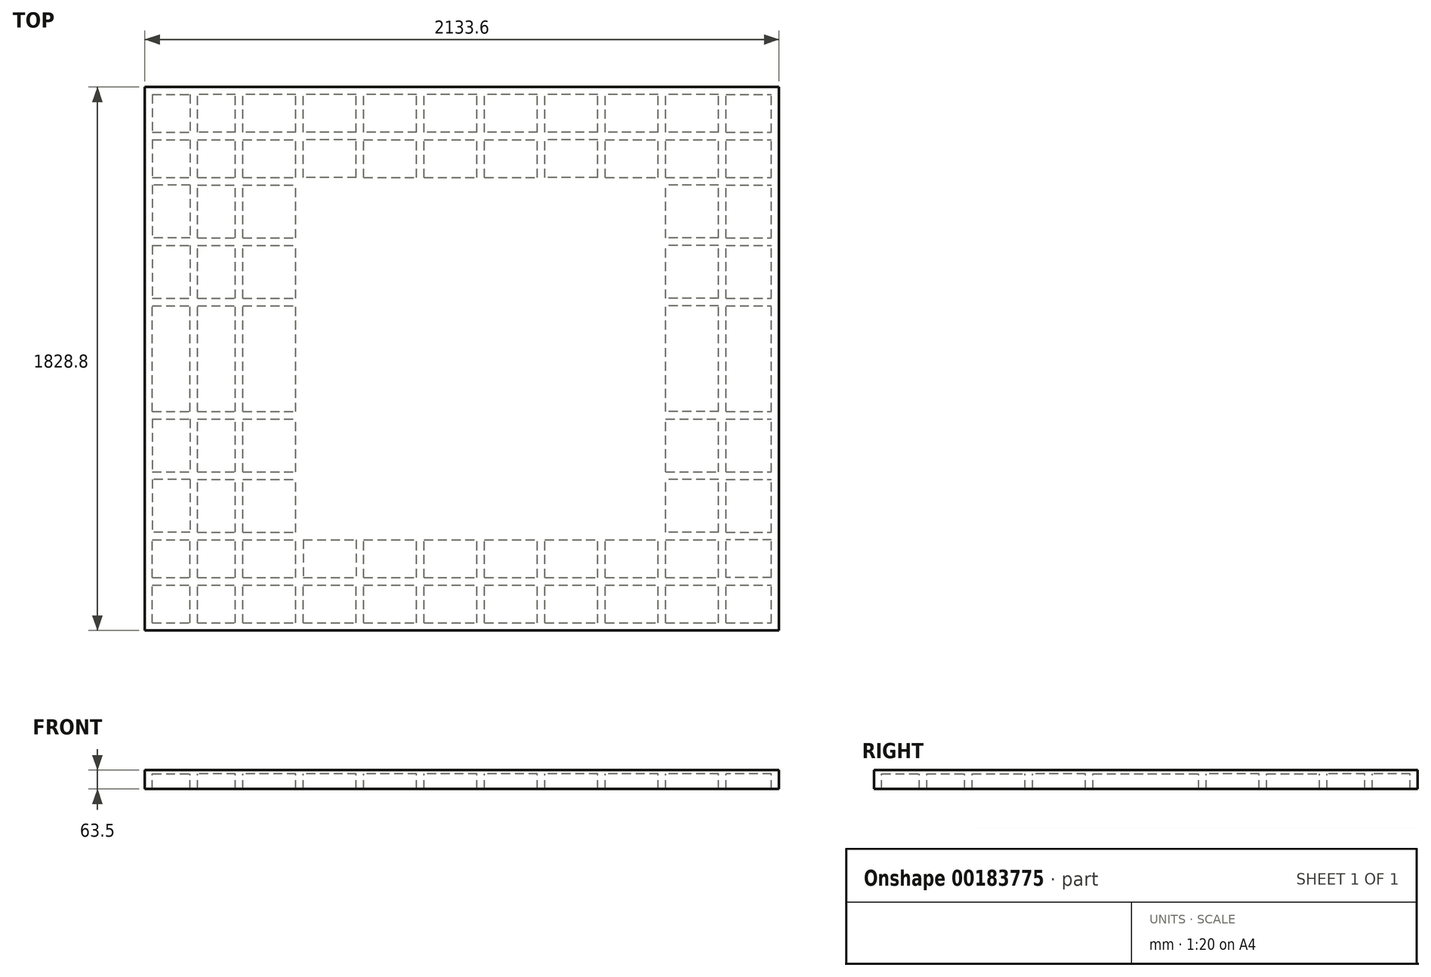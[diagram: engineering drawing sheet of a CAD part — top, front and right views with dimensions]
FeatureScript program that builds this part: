
annotation { "Feature Type Name" : "Feature", "Feature Type Description" : "" }
export const myFeature = defineFeature(function(context is Context, id is Id, definition is map)
    precondition{}
    {
        {
            var Q0;
            Q0=qCreatedBy(makeId("Top.planeOp"),FACE);
            var sketch = newSketch(context, id + "F0", { "sketchPlane" : qUnion([Q0])});
            skLineSegment(sketch, "E0.bottom", {"start": v(0, 0) * mm, "end": v(-2133.6, 0) * mm});
            skLineSegment(sketch, "E0.top", {"start": v(0, 1828.8) * mm, "end": v(-2133.6, 1828.8) * mm});
            skLineSegment(sketch, "E0.left", {"start": v(0, 0) * mm, "end": v(0, 1828.8) * mm});
            skLineSegment(sketch, "E0.right", {"start": v(-2133.6, 0) * mm, "end": v(-2133.6, 1828.8) * mm});
            skSolve(sketch);
        }
        {
            var Q0;
            Q0 = qSketchRegion(id + "F0", true);
            extrude(context, id + "F1", {"entities" : qUnion([Q0]), "oppositeDirection" : true, "depth" : 12.7 * mm});
        }
        {
            var Q0;
            Q0=makeQuery(id+"F1.opExtrude","CAP_FACE",FACE,{"disambiguationData":[OSD([sQuery(id+"F0.wireOp",EDGE,"E0.bottom"),sQuery(id+"F0.wireOp",EDGE,"E0.top"),sQuery(id+"F0.wireOp",EDGE,"E0.left"),sQuery(id+"F0.wireOp",EDGE,"E0.right")])],"isStart":false});
            var sketch = newSketch(context, id + "F2", { "sketchPlane" : qUnion([Q0])});
            skLineSegment(sketch, "E1", {"start": v(-2133.6, 0) * mm, "end": v(-2133.6, -1828.8) * mm});
            skLineSegment(sketch, "E2", {"start": v(-2133.6, -1828.8) * mm, "end": v(0, -1828.8) * mm});
            skLineSegment(sketch, "E3", {"start": v(0, -1828.8) * mm, "end": v(0, 0) * mm});
            skLineSegment(sketch, "E4", {"start": v(0, 0) * mm, "end": v(-2133.6, 0) * mm});
            skLineSegment(sketch, "E5", {"start": v(-2133.6, -25.4) * mm, "end": v(0, -25.4) * mm, "construction": true});
            skLineSegment(sketch, "E6", {"start": v(-2133.6, -1803.4) * mm, "end": v(0, -1803.4) * mm, "construction": true});
            skLineSegment(sketch, "E7", {"start": v(-25.4, 0) * mm, "end": v(-25.4, -1828.8) * mm, "construction": true});
            skLineSegment(sketch, "E8", {"start": v(-2108.2, 0) * mm, "end": v(-2108.2, -1828.8) * mm, "construction": true});
            skLineSegment(sketch, "E9", {"start": v(-2133.6, -152.4) * mm, "end": v(0, -152.4) * mm, "construction": true});
            skLineSegment(sketch, "E10", {"start": v(-2133.6, -304.8) * mm, "end": v(0, -304.8) * mm, "construction": true});
            skLineSegment(sketch, "E11", {"start": v(-2133.6, -508) * mm, "end": v(0, -508) * mm, "construction": true});
            skLineSegment(sketch, "E12", {"start": v(-609.6, 0) * mm, "end": v(-609.6, -1828.8) * mm, "construction": true});
            skLineSegment(sketch, "E13", {"start": v(-812.8, 0) * mm, "end": v(-812.8, -1828.8) * mm, "construction": true});
            skLineSegment(sketch, "E14", {"start": v(-1981.2, 0) * mm, "end": v(-1981.2, -1828.8) * mm, "construction": true});
            skLineSegment(sketch, "E15", {"start": v(-1828.8, 0) * mm, "end": v(-1828.8, -1828.8) * mm, "construction": true});
            skLineSegment(sketch, "E16", {"start": v(-1625.6, 0) * mm, "end": v(-1625.6, -1828.8) * mm, "construction": true});
            skLineSegment(sketch, "E17", {"start": v(-1422.4, 0) * mm, "end": v(-1422.4, -1828.8) * mm, "construction": true});
            skLineSegment(sketch, "E18", {"start": v(-1219.2, 0) * mm, "end": v(-1219.2, -1828.8) * mm, "construction": true});
            skLineSegment(sketch, "E19", {"start": v(-1016, 0) * mm, "end": v(-1016, -1828.8) * mm, "construction": true});
            skLineSegment(sketch, "E20", {"start": v(-406.4, 0) * mm, "end": v(-406.4, -1828.8) * mm, "construction": true});
            skLineSegment(sketch, "E21", {"start": v(-203.2, 0) * mm, "end": v(-203.2, -1828.8) * mm, "construction": true});
            skLineSegment(sketch, "E22", {"start": v(0, -1676.4) * mm, "end": v(-2133.6, -1676.4) * mm, "construction": true});
            skLineSegment(sketch, "E23", {"start": v(-2133.6, -1524) * mm, "end": v(0, -1524) * mm, "construction": true});
            skLineSegment(sketch, "E24", {"start": v(-2133.6, -1320.8) * mm, "end": v(0, -1320.8) * mm, "construction": true});
            skLineSegment(sketch, "E25", {"start": v(0, -711.2) * mm, "end": v(-2133.6, -711.2) * mm, "construction": true});
            skLineSegment(sketch, "E26", {"start": v(0, -1117.6) * mm, "end": v(-2133.6, -1117.6) * mm, "construction": true});
            skLineSegment(sketch, "E27.bottom", {"start": v(-2108.2, -25.4) * mm, "end": v(-1981.2, -25.4) * mm});
            skLineSegment(sketch, "E27.top", {"start": v(-2108.2, -152.4) * mm, "end": v(-1981.2, -152.4) * mm});
            skLineSegment(sketch, "E27.left", {"start": v(-2108.2, -25.4) * mm, "end": v(-2108.2, -152.4) * mm});
            skLineSegment(sketch, "E27.right", {"start": v(-1981.2, -25.4) * mm, "end": v(-1981.2, -152.4) * mm});
            skLineSegment(sketch, "E28.bottom", {"start": v(-2108.2, -1803.4) * mm, "end": v(-1981.2, -1803.4) * mm});
            skLineSegment(sketch, "E28.top", {"start": v(-2108.2, -1676.4) * mm, "end": v(-1981.2, -1676.4) * mm});
            skLineSegment(sketch, "E28.left", {"start": v(-2108.2, -1803.4) * mm, "end": v(-2108.2, -1676.4) * mm});
            skLineSegment(sketch, "E28.right", {"start": v(-1981.2, -1803.4) * mm, "end": v(-1981.2, -1676.4) * mm});
            skLineSegment(sketch, "E29", {"start": v(-1955.8, -1828.8) * mm, "end": v(-1955.8, 0) * mm, "construction": true});
            skLineSegment(sketch, "E30", {"start": v(-1803.4, 0) * mm, "end": v(-1803.4, -1828.8) * mm, "construction": true});
            skLineSegment(sketch, "E31", {"start": v(-1600.2, 0) * mm, "end": v(-1600.2, -1828.8) * mm, "construction": true});
            skLineSegment(sketch, "E32", {"start": v(-1600.2, -1828.8) * mm, "end": v(-1397, -1828.8) * mm, "construction": true});
            skLineSegment(sketch, "E33", {"start": v(-1397, -1828.8) * mm, "end": v(-1397, 0) * mm, "construction": true});
            skLineSegment(sketch, "E34", {"start": v(-1397, 0) * mm, "end": v(-1193.8, 0) * mm, "construction": true});
            skLineSegment(sketch, "E35", {"start": v(-1193.8, 0) * mm, "end": v(-1193.8, -1828.8) * mm, "construction": true});
            skLineSegment(sketch, "E36", {"start": v(-1193.8, -1828.8) * mm, "end": v(-990.6, -1828.8) * mm, "construction": true});
            skLineSegment(sketch, "E37", {"start": v(-990.6, -1828.8) * mm, "end": v(-990.6, 0) * mm, "construction": true});
            skLineSegment(sketch, "E38", {"start": v(-990.6, 0) * mm, "end": v(-787.4, 0) * mm, "construction": true});
            skLineSegment(sketch, "E39", {"start": v(-787.4, 0) * mm, "end": v(-787.4, -1828.8) * mm, "construction": true});
            skLineSegment(sketch, "E40", {"start": v(-787.4, -1828.8) * mm, "end": v(-584.2, -1828.8) * mm, "construction": true});
            skLineSegment(sketch, "E41", {"start": v(-584.2, -1828.8) * mm, "end": v(-584.2, -25.4) * mm, "construction": true});
            skLineSegment(sketch, "E42", {"start": v(-584.2, -25.4) * mm, "end": v(-381, -25.4) * mm, "construction": true});
            skLineSegment(sketch, "E43", {"start": v(-381, -25.4) * mm, "end": v(-381, -1828.8) * mm, "construction": true});
            skLineSegment(sketch, "E44", {"start": v(-381, -1828.8) * mm, "end": v(-177.8, -1828.8) * mm, "construction": true});
            skLineSegment(sketch, "E45", {"start": v(-177.8, -1828.8) * mm, "end": v(-177.8, -25.4) * mm, "construction": true});
            skLineSegment(sketch, "E46", {"start": v(-2133.6, -177.8) * mm, "end": v(0, -177.8) * mm, "construction": true});
            skLineSegment(sketch, "E47", {"start": v(0, -177.8) * mm, "end": v(0, -330.2) * mm, "construction": true});
            skLineSegment(sketch, "E48", {"start": v(0, -330.2) * mm, "end": v(-2133.6, -330.2) * mm, "construction": true});
            skLineSegment(sketch, "E49", {"start": v(-2133.6, -330.2) * mm, "end": v(-2133.6, -533.4) * mm, "construction": true});
            skLineSegment(sketch, "E50", {"start": v(-2133.6, -533.4) * mm, "end": v(0, -533.4) * mm, "construction": true});
            skLineSegment(sketch, "E51", {"start": v(0, -533.4) * mm, "end": v(0, -736.6) * mm, "construction": true});
            skLineSegment(sketch, "E52", {"start": v(0, -736.6) * mm, "end": v(-2133.6, -736.6) * mm, "construction": true});
            skLineSegment(sketch, "E53", {"start": v(-2133.6, -736.6) * mm, "end": v(-2133.6, -1092.2) * mm, "construction": true});
            skLineSegment(sketch, "E54", {"start": v(-2133.6, -1092.2) * mm, "end": v(0, -1092.2) * mm, "construction": true});
            skLineSegment(sketch, "E55", {"start": v(0, -1092.2) * mm, "end": v(0, -1295.4) * mm, "construction": true});
            skLineSegment(sketch, "E56", {"start": v(0, -1295.4) * mm, "end": v(-2133.6, -1295.4) * mm, "construction": true});
            skLineSegment(sketch, "E57", {"start": v(-2133.6, -1295.4) * mm, "end": v(-2133.6, -1498.6) * mm, "construction": true});
            skLineSegment(sketch, "E58", {"start": v(-2133.6, -1498.6) * mm, "end": v(0, -1498.6) * mm, "construction": true});
            skLineSegment(sketch, "E59", {"start": v(0, -1498.6) * mm, "end": v(0, -1651) * mm, "construction": true});
            skLineSegment(sketch, "E60", {"start": v(0, -1651) * mm, "end": v(-2133.6, -1651) * mm, "construction": true});
            skLineSegment(sketch, "E61.bottom", {"start": v(-1955.8, -25.4) * mm, "end": v(-1828.8, -25.4) * mm});
            skLineSegment(sketch, "E61.top", {"start": v(-1955.8, -152.4) * mm, "end": v(-1828.8, -152.4) * mm});
            skLineSegment(sketch, "E61.left", {"start": v(-1955.8, -25.4) * mm, "end": v(-1955.8, -152.4) * mm});
            skLineSegment(sketch, "E61.right", {"start": v(-1828.8, -25.4) * mm, "end": v(-1828.8, -152.4) * mm});
            skLineSegment(sketch, "E62.bottom", {"start": v(-1803.4, -25.4) * mm, "end": v(-1625.6, -25.4) * mm});
            skLineSegment(sketch, "E62.top", {"start": v(-1803.4, -152.4) * mm, "end": v(-1625.6, -152.4) * mm});
            skLineSegment(sketch, "E62.left", {"start": v(-1803.4, -25.4) * mm, "end": v(-1803.4, -152.4) * mm});
            skLineSegment(sketch, "E62.right", {"start": v(-1625.6, -25.4) * mm, "end": v(-1625.6, -152.4) * mm});
            skLineSegment(sketch, "E63.bottom", {"start": v(-1600.2, -25.4) * mm, "end": v(-1422.4, -25.4) * mm});
            skLineSegment(sketch, "E63.top", {"start": v(-1600.2, -152.4) * mm, "end": v(-1422.4, -152.4) * mm});
            skLineSegment(sketch, "E63.left", {"start": v(-1600.2, -25.4) * mm, "end": v(-1600.2, -152.4) * mm});
            skLineSegment(sketch, "E63.right", {"start": v(-1422.4, -25.4) * mm, "end": v(-1422.4, -152.4) * mm});
            skLineSegment(sketch, "E64.bottom", {"start": v(-1397, -25.4) * mm, "end": v(-1219.2, -25.4) * mm});
            skLineSegment(sketch, "E64.top", {"start": v(-1397, -152.4) * mm, "end": v(-1219.2, -152.4) * mm});
            skLineSegment(sketch, "E64.left", {"start": v(-1397, -25.4) * mm, "end": v(-1397, -152.4) * mm});
            skLineSegment(sketch, "E64.right", {"start": v(-1219.2, -25.4) * mm, "end": v(-1219.2, -152.4) * mm});
            skLineSegment(sketch, "E65.bottom", {"start": v(-1193.8, -25.4) * mm, "end": v(-1016, -25.4) * mm});
            skLineSegment(sketch, "E65.top", {"start": v(-1193.8, -152.4) * mm, "end": v(-1016, -152.4) * mm});
            skLineSegment(sketch, "E65.left", {"start": v(-1193.8, -25.4) * mm, "end": v(-1193.8, -152.4) * mm});
            skLineSegment(sketch, "E65.right", {"start": v(-1016, -25.4) * mm, "end": v(-1016, -152.4) * mm});
            skLineSegment(sketch, "E66.bottom", {"start": v(-990.6, -25.4) * mm, "end": v(-812.8, -25.4) * mm});
            skLineSegment(sketch, "E66.top", {"start": v(-990.6, -152.4) * mm, "end": v(-812.8, -152.4) * mm});
            skLineSegment(sketch, "E66.left", {"start": v(-990.6, -25.4) * mm, "end": v(-990.6, -152.4) * mm});
            skLineSegment(sketch, "E66.right", {"start": v(-812.8, -25.4) * mm, "end": v(-812.8, -152.4) * mm});
            skLineSegment(sketch, "E67.bottom", {"start": v(-787.4, -25.4) * mm, "end": v(-609.6, -25.4) * mm});
            skLineSegment(sketch, "E67.top", {"start": v(-787.4, -152.4) * mm, "end": v(-609.6, -152.4) * mm});
            skLineSegment(sketch, "E67.left", {"start": v(-787.4, -25.4) * mm, "end": v(-787.4, -152.4) * mm});
            skLineSegment(sketch, "E67.right", {"start": v(-609.6, -25.4) * mm, "end": v(-609.6, -152.4) * mm});
            skLineSegment(sketch, "E68.bottom", {"start": v(-584.2, -25.4) * mm, "end": v(-406.4, -25.4) * mm});
            skLineSegment(sketch, "E68.top", {"start": v(-584.2, -152.4) * mm, "end": v(-406.4, -152.4) * mm});
            skLineSegment(sketch, "E68.left", {"start": v(-584.2, -25.4) * mm, "end": v(-584.2, -152.4) * mm});
            skLineSegment(sketch, "E68.right", {"start": v(-406.4, -25.4) * mm, "end": v(-406.4, -152.4) * mm});
            skLineSegment(sketch, "E69.bottom", {"start": v(-381, -25.4) * mm, "end": v(-203.2, -25.4) * mm});
            skLineSegment(sketch, "E69.top", {"start": v(-381, -152.4) * mm, "end": v(-203.2, -152.4) * mm});
            skLineSegment(sketch, "E69.left", {"start": v(-381, -25.4) * mm, "end": v(-381, -152.4) * mm});
            skLineSegment(sketch, "E69.right", {"start": v(-203.2, -25.4) * mm, "end": v(-203.2, -152.4) * mm});
            skLineSegment(sketch, "E70.bottom", {"start": v(-177.8, -25.4) * mm, "end": v(-25.4, -25.4) * mm});
            skLineSegment(sketch, "E70.top", {"start": v(-177.8, -152.4) * mm, "end": v(-25.4, -152.4) * mm});
            skLineSegment(sketch, "E70.left", {"start": v(-177.8, -25.4) * mm, "end": v(-177.8, -152.4) * mm});
            skLineSegment(sketch, "E70.right", {"start": v(-25.4, -25.4) * mm, "end": v(-25.4, -152.4) * mm});
            skLineSegment(sketch, "E71.bottom", {"start": v(-25.4, -177.8) * mm, "end": v(-177.8, -177.8) * mm});
            skLineSegment(sketch, "E71.top", {"start": v(-25.4, -304.8) * mm, "end": v(-177.8, -304.8) * mm});
            skLineSegment(sketch, "E71.left", {"start": v(-25.4, -177.8) * mm, "end": v(-25.4, -304.8) * mm});
            skLineSegment(sketch, "E71.right", {"start": v(-177.8, -177.8) * mm, "end": v(-177.8, -304.8) * mm});
            skLineSegment(sketch, "E72.bottom", {"start": v(-177.8, -330.2) * mm, "end": v(-25.4, -330.2) * mm});
            skLineSegment(sketch, "E72.top", {"start": v(-177.8, -508) * mm, "end": v(-25.4, -508) * mm});
            skLineSegment(sketch, "E72.left", {"start": v(-177.8, -330.2) * mm, "end": v(-177.8, -508) * mm});
            skLineSegment(sketch, "E72.right", {"start": v(-25.4, -330.2) * mm, "end": v(-25.4, -508) * mm});
            skLineSegment(sketch, "E73.bottom", {"start": v(-177.8, -533.4) * mm, "end": v(-25.4, -533.4) * mm});
            skLineSegment(sketch, "E73.top", {"start": v(-177.8, -711.2) * mm, "end": v(-25.4, -711.2) * mm});
            skLineSegment(sketch, "E73.left", {"start": v(-177.8, -533.4) * mm, "end": v(-177.8, -711.2) * mm});
            skLineSegment(sketch, "E73.right", {"start": v(-25.4, -533.4) * mm, "end": v(-25.4, -711.2) * mm});
            skLineSegment(sketch, "E74.bottom", {"start": v(-177.8, -736.6) * mm, "end": v(-25.4, -736.6) * mm});
            skLineSegment(sketch, "E74.top", {"start": v(-177.8, -1092.2) * mm, "end": v(-25.4, -1092.2) * mm});
            skLineSegment(sketch, "E74.left", {"start": v(-177.8, -736.6) * mm, "end": v(-177.8, -1092.2) * mm});
            skLineSegment(sketch, "E74.right", {"start": v(-25.4, -736.6) * mm, "end": v(-25.4, -1092.2) * mm});
            skLineSegment(sketch, "E75.bottom", {"start": v(-177.8, -1117.6) * mm, "end": v(-25.4, -1117.6) * mm});
            skLineSegment(sketch, "E75.top", {"start": v(-177.8, -1295.4) * mm, "end": v(-25.4, -1295.4) * mm});
            skLineSegment(sketch, "E75.left", {"start": v(-177.8, -1117.6) * mm, "end": v(-177.8, -1295.4) * mm});
            skLineSegment(sketch, "E75.right", {"start": v(-25.4, -1117.6) * mm, "end": v(-25.4, -1295.4) * mm});
            skLineSegment(sketch, "E76.bottom", {"start": v(-177.8, -1320.8) * mm, "end": v(-25.4, -1320.8) * mm});
            skLineSegment(sketch, "E76.top", {"start": v(-177.8, -1498.6) * mm, "end": v(-25.4, -1498.6) * mm});
            skLineSegment(sketch, "E76.left", {"start": v(-177.8, -1320.8) * mm, "end": v(-177.8, -1498.6) * mm});
            skLineSegment(sketch, "E76.right", {"start": v(-25.4, -1320.8) * mm, "end": v(-25.4, -1498.6) * mm});
            skLineSegment(sketch, "E77.bottom", {"start": v(-177.8, -1524) * mm, "end": v(-25.4, -1524) * mm});
            skLineSegment(sketch, "E77.top", {"start": v(-177.8, -1651) * mm, "end": v(-25.4, -1651) * mm});
            skLineSegment(sketch, "E77.left", {"start": v(-177.8, -1524) * mm, "end": v(-177.8, -1651) * mm});
            skLineSegment(sketch, "E77.right", {"start": v(-25.4, -1524) * mm, "end": v(-25.4, -1651) * mm});
            skLineSegment(sketch, "E78.bottom", {"start": v(-177.8, -1676.4) * mm, "end": v(-25.4, -1676.4) * mm});
            skLineSegment(sketch, "E78.top", {"start": v(-177.8, -1803.4) * mm, "end": v(-25.4, -1803.4) * mm});
            skLineSegment(sketch, "E78.left", {"start": v(-177.8, -1676.4) * mm, "end": v(-177.8, -1803.4) * mm});
            skLineSegment(sketch, "E78.right", {"start": v(-25.4, -1676.4) * mm, "end": v(-25.4, -1803.4) * mm});
            skLineSegment(sketch, "E79.bottom", {"start": v(-203.2, -1676.4) * mm, "end": v(-381, -1676.4) * mm});
            skLineSegment(sketch, "E79.top", {"start": v(-203.2, -1803.4) * mm, "end": v(-381, -1803.4) * mm});
            skLineSegment(sketch, "E79.left", {"start": v(-203.2, -1676.4) * mm, "end": v(-203.2, -1803.4) * mm});
            skLineSegment(sketch, "E79.right", {"start": v(-381, -1676.4) * mm, "end": v(-381, -1803.4) * mm});
            skLineSegment(sketch, "E80.bottom", {"start": v(-406.4, -1676.4) * mm, "end": v(-584.2, -1676.4) * mm});
            skLineSegment(sketch, "E80.top", {"start": v(-406.4, -1803.4) * mm, "end": v(-584.2, -1803.4) * mm});
            skLineSegment(sketch, "E80.left", {"start": v(-406.4, -1676.4) * mm, "end": v(-406.4, -1803.4) * mm});
            skLineSegment(sketch, "E80.right", {"start": v(-584.2, -1676.4) * mm, "end": v(-584.2, -1803.4) * mm});
            skLineSegment(sketch, "E81.bottom", {"start": v(-609.6, -1676.4) * mm, "end": v(-787.4, -1676.4) * mm});
            skLineSegment(sketch, "E81.top", {"start": v(-609.6, -1803.4) * mm, "end": v(-787.4, -1803.4) * mm});
            skLineSegment(sketch, "E81.left", {"start": v(-609.6, -1676.4) * mm, "end": v(-609.6, -1803.4) * mm});
            skLineSegment(sketch, "E81.right", {"start": v(-787.4, -1676.4) * mm, "end": v(-787.4, -1803.4) * mm});
            skLineSegment(sketch, "E82.bottom", {"start": v(-812.8, -1676.4) * mm, "end": v(-990.6, -1676.4) * mm});
            skLineSegment(sketch, "E82.top", {"start": v(-812.8, -1803.4) * mm, "end": v(-990.6, -1803.4) * mm});
            skLineSegment(sketch, "E82.left", {"start": v(-812.8, -1676.4) * mm, "end": v(-812.8, -1803.4) * mm});
            skLineSegment(sketch, "E82.right", {"start": v(-990.6, -1676.4) * mm, "end": v(-990.6, -1803.4) * mm});
            skLineSegment(sketch, "E83.bottom", {"start": v(-1016, -1676.4) * mm, "end": v(-1193.8, -1676.4) * mm});
            skLineSegment(sketch, "E83.top", {"start": v(-1016, -1803.4) * mm, "end": v(-1193.8, -1803.4) * mm});
            skLineSegment(sketch, "E83.left", {"start": v(-1016, -1676.4) * mm, "end": v(-1016, -1803.4) * mm});
            skLineSegment(sketch, "E83.right", {"start": v(-1193.8, -1676.4) * mm, "end": v(-1193.8, -1803.4) * mm});
            skLineSegment(sketch, "E84.bottom", {"start": v(-1219.2, -1676.4) * mm, "end": v(-1397, -1676.4) * mm});
            skLineSegment(sketch, "E84.top", {"start": v(-1219.2, -1803.4) * mm, "end": v(-1397, -1803.4) * mm});
            skLineSegment(sketch, "E84.left", {"start": v(-1219.2, -1676.4) * mm, "end": v(-1219.2, -1803.4) * mm});
            skLineSegment(sketch, "E84.right", {"start": v(-1397, -1676.4) * mm, "end": v(-1397, -1803.4) * mm});
            skLineSegment(sketch, "E85.bottom", {"start": v(-1422.4, -1676.4) * mm, "end": v(-1600.2, -1676.4) * mm});
            skLineSegment(sketch, "E85.top", {"start": v(-1422.4, -1803.4) * mm, "end": v(-1600.2, -1803.4) * mm});
            skLineSegment(sketch, "E85.left", {"start": v(-1422.4, -1676.4) * mm, "end": v(-1422.4, -1803.4) * mm});
            skLineSegment(sketch, "E85.right", {"start": v(-1600.2, -1676.4) * mm, "end": v(-1600.2, -1803.4) * mm});
            skLineSegment(sketch, "E86.bottom", {"start": v(-1625.6, -1676.4) * mm, "end": v(-1803.4, -1676.4) * mm});
            skLineSegment(sketch, "E86.top", {"start": v(-1625.6, -1803.4) * mm, "end": v(-1803.4, -1803.4) * mm});
            skLineSegment(sketch, "E86.left", {"start": v(-1625.6, -1676.4) * mm, "end": v(-1625.6, -1803.4) * mm});
            skLineSegment(sketch, "E86.right", {"start": v(-1803.4, -1676.4) * mm, "end": v(-1803.4, -1803.4) * mm});
            skLineSegment(sketch, "E87.bottom", {"start": v(-1828.8, -1676.4) * mm, "end": v(-1955.8, -1676.4) * mm});
            skLineSegment(sketch, "E87.top", {"start": v(-1828.8, -1803.4) * mm, "end": v(-1955.8, -1803.4) * mm});
            skLineSegment(sketch, "E87.left", {"start": v(-1828.8, -1676.4) * mm, "end": v(-1828.8, -1803.4) * mm});
            skLineSegment(sketch, "E87.right", {"start": v(-1955.8, -1676.4) * mm, "end": v(-1955.8, -1803.4) * mm});
            skLineSegment(sketch, "E88.bottom", {"start": v(-2108.2, -1651) * mm, "end": v(-1981.2, -1651) * mm});
            skLineSegment(sketch, "E88.top", {"start": v(-2108.2, -1524) * mm, "end": v(-1981.2, -1524) * mm});
            skLineSegment(sketch, "E88.left", {"start": v(-2108.2, -1651) * mm, "end": v(-2108.2, -1524) * mm});
            skLineSegment(sketch, "E88.right", {"start": v(-1981.2, -1651) * mm, "end": v(-1981.2, -1524) * mm});
            skLineSegment(sketch, "E89.bottom", {"start": v(-1981.2, -1498.6) * mm, "end": v(-2108.2, -1498.6) * mm});
            skLineSegment(sketch, "E89.top", {"start": v(-1981.2, -1320.8) * mm, "end": v(-2108.2, -1320.8) * mm});
            skLineSegment(sketch, "E89.left", {"start": v(-1981.2, -1498.6) * mm, "end": v(-1981.2, -1320.8) * mm});
            skLineSegment(sketch, "E89.right", {"start": v(-2108.2, -1498.6) * mm, "end": v(-2108.2, -1320.8) * mm});
            skLineSegment(sketch, "E90.bottom", {"start": v(-2108.2, -1295.4) * mm, "end": v(-1981.2, -1295.4) * mm});
            skLineSegment(sketch, "E90.top", {"start": v(-2108.2, -1117.6) * mm, "end": v(-1981.2, -1117.6) * mm});
            skLineSegment(sketch, "E90.left", {"start": v(-2108.2, -1295.4) * mm, "end": v(-2108.2, -1117.6) * mm});
            skLineSegment(sketch, "E90.right", {"start": v(-1981.2, -1295.4) * mm, "end": v(-1981.2, -1117.6) * mm});
            skLineSegment(sketch, "E91.bottom", {"start": v(-2108.2, -736.6) * mm, "end": v(-1981.2, -736.6) * mm});
            skLineSegment(sketch, "E91.top", {"start": v(-2108.2, -1092.2) * mm, "end": v(-1981.2, -1092.2) * mm});
            skLineSegment(sketch, "E91.left", {"start": v(-2108.2, -736.6) * mm, "end": v(-2108.2, -1092.2) * mm});
            skLineSegment(sketch, "E91.right", {"start": v(-1981.2, -736.6) * mm, "end": v(-1981.2, -1092.2) * mm});
            skLineSegment(sketch, "E92.bottom", {"start": v(-2108.2, -711.2) * mm, "end": v(-1981.2, -711.2) * mm});
            skLineSegment(sketch, "E92.top", {"start": v(-2108.2, -533.4) * mm, "end": v(-1981.2, -533.4) * mm});
            skLineSegment(sketch, "E92.left", {"start": v(-2108.2, -711.2) * mm, "end": v(-2108.2, -533.4) * mm});
            skLineSegment(sketch, "E92.right", {"start": v(-1981.2, -711.2) * mm, "end": v(-1981.2, -533.4) * mm});
            skLineSegment(sketch, "E93.bottom", {"start": v(-1981.2, -508) * mm, "end": v(-2108.2, -508) * mm});
            skLineSegment(sketch, "E93.top", {"start": v(-1981.2, -330.2) * mm, "end": v(-2108.2, -330.2) * mm});
            skLineSegment(sketch, "E93.left", {"start": v(-1981.2, -508) * mm, "end": v(-1981.2, -330.2) * mm});
            skLineSegment(sketch, "E93.right", {"start": v(-2108.2, -508) * mm, "end": v(-2108.2, -330.2) * mm});
            skLineSegment(sketch, "E94.bottom", {"start": v(-2108.2, -177.8) * mm, "end": v(-1981.2, -177.8) * mm});
            skLineSegment(sketch, "E94.top", {"start": v(-2108.2, -304.8) * mm, "end": v(-1981.2, -304.8) * mm});
            skLineSegment(sketch, "E94.left", {"start": v(-2108.2, -177.8) * mm, "end": v(-2108.2, -304.8) * mm});
            skLineSegment(sketch, "E94.right", {"start": v(-1981.2, -177.8) * mm, "end": v(-1981.2, -304.8) * mm});
            skLineSegment(sketch, "E95.bottom", {"start": v(-1955.8, -177.8) * mm, "end": v(-1828.8, -177.8) * mm});
            skLineSegment(sketch, "E95.top", {"start": v(-1955.8, -304.8) * mm, "end": v(-1828.8, -304.8) * mm});
            skLineSegment(sketch, "E95.left", {"start": v(-1955.8, -177.8) * mm, "end": v(-1955.8, -304.8) * mm});
            skLineSegment(sketch, "E95.right", {"start": v(-1828.8, -177.8) * mm, "end": v(-1828.8, -304.8) * mm});
            skLineSegment(sketch, "E96.bottom", {"start": v(-1955.8, -330.2) * mm, "end": v(-1828.8, -330.2) * mm});
            skLineSegment(sketch, "E96.top", {"start": v(-1955.8, -508) * mm, "end": v(-1828.8, -508) * mm});
            skLineSegment(sketch, "E96.left", {"start": v(-1955.8, -330.2) * mm, "end": v(-1955.8, -508) * mm});
            skLineSegment(sketch, "E96.right", {"start": v(-1828.8, -330.2) * mm, "end": v(-1828.8, -508) * mm});
            skLineSegment(sketch, "E97.bottom", {"start": v(-1955.8, -533.4) * mm, "end": v(-1828.8, -533.4) * mm});
            skLineSegment(sketch, "E97.top", {"start": v(-1955.8, -711.2) * mm, "end": v(-1828.8, -711.2) * mm});
            skLineSegment(sketch, "E97.left", {"start": v(-1955.8, -533.4) * mm, "end": v(-1955.8, -711.2) * mm});
            skLineSegment(sketch, "E97.right", {"start": v(-1828.8, -533.4) * mm, "end": v(-1828.8, -711.2) * mm});
            skLineSegment(sketch, "E98.bottom", {"start": v(-1955.8, -736.6) * mm, "end": v(-1828.8, -736.6) * mm});
            skLineSegment(sketch, "E98.top", {"start": v(-1955.8, -1092.2) * mm, "end": v(-1828.8, -1092.2) * mm});
            skLineSegment(sketch, "E98.left", {"start": v(-1955.8, -736.6) * mm, "end": v(-1955.8, -1092.2) * mm});
            skLineSegment(sketch, "E98.right", {"start": v(-1828.8, -736.6) * mm, "end": v(-1828.8, -1092.2) * mm});
            skLineSegment(sketch, "E99.bottom", {"start": v(-1955.8, -1117.6) * mm, "end": v(-1828.8, -1117.6) * mm});
            skLineSegment(sketch, "E99.top", {"start": v(-1955.8, -1295.4) * mm, "end": v(-1828.8, -1295.4) * mm});
            skLineSegment(sketch, "E99.left", {"start": v(-1955.8, -1117.6) * mm, "end": v(-1955.8, -1295.4) * mm});
            skLineSegment(sketch, "E99.right", {"start": v(-1828.8, -1117.6) * mm, "end": v(-1828.8, -1295.4) * mm});
            skLineSegment(sketch, "E100.bottom", {"start": v(-1955.8, -1320.8) * mm, "end": v(-1828.8, -1320.8) * mm});
            skLineSegment(sketch, "E100.top", {"start": v(-1955.8, -1498.6) * mm, "end": v(-1828.8, -1498.6) * mm});
            skLineSegment(sketch, "E100.left", {"start": v(-1955.8, -1320.8) * mm, "end": v(-1955.8, -1498.6) * mm});
            skLineSegment(sketch, "E100.right", {"start": v(-1828.8, -1320.8) * mm, "end": v(-1828.8, -1498.6) * mm});
            skLineSegment(sketch, "E101.bottom", {"start": v(-1955.8, -1524) * mm, "end": v(-1828.8, -1524) * mm});
            skLineSegment(sketch, "E101.top", {"start": v(-1955.8, -1651) * mm, "end": v(-1828.8, -1651) * mm});
            skLineSegment(sketch, "E101.left", {"start": v(-1955.8, -1524) * mm, "end": v(-1955.8, -1651) * mm});
            skLineSegment(sketch, "E101.right", {"start": v(-1828.8, -1524) * mm, "end": v(-1828.8, -1651) * mm});
            skLineSegment(sketch, "E102.bottom", {"start": v(-1803.4, -177.8) * mm, "end": v(-1625.6, -177.8) * mm});
            skLineSegment(sketch, "E102.top", {"start": v(-1803.4, -304.8) * mm, "end": v(-1625.6, -304.8) * mm});
            skLineSegment(sketch, "E102.left", {"start": v(-1803.4, -177.8) * mm, "end": v(-1803.4, -304.8) * mm});
            skLineSegment(sketch, "E102.right", {"start": v(-1625.6, -177.8) * mm, "end": v(-1625.6, -304.8) * mm});
            skLineSegment(sketch, "E103.bottom", {"start": v(-1803.4, -330.2) * mm, "end": v(-1625.6, -330.2) * mm});
            skLineSegment(sketch, "E103.top", {"start": v(-1803.4, -508) * mm, "end": v(-1625.6, -508) * mm});
            skLineSegment(sketch, "E103.left", {"start": v(-1803.4, -330.2) * mm, "end": v(-1803.4, -508) * mm});
            skLineSegment(sketch, "E103.right", {"start": v(-1625.6, -330.2) * mm, "end": v(-1625.6, -508) * mm});
            skLineSegment(sketch, "E104.bottom", {"start": v(-1803.4, -533.4) * mm, "end": v(-1625.6, -533.4) * mm});
            skLineSegment(sketch, "E104.top", {"start": v(-1803.4, -711.2) * mm, "end": v(-1625.6, -711.2) * mm});
            skLineSegment(sketch, "E104.left", {"start": v(-1803.4, -533.4) * mm, "end": v(-1803.4, -711.2) * mm});
            skLineSegment(sketch, "E104.right", {"start": v(-1625.6, -533.4) * mm, "end": v(-1625.6, -711.2) * mm});
            skLineSegment(sketch, "E105.bottom", {"start": v(-1803.4, -736.6) * mm, "end": v(-1625.6, -736.6) * mm});
            skLineSegment(sketch, "E105.top", {"start": v(-1803.4, -1092.2) * mm, "end": v(-1625.6, -1092.2) * mm});
            skLineSegment(sketch, "E105.left", {"start": v(-1803.4, -736.6) * mm, "end": v(-1803.4, -1092.2) * mm});
            skLineSegment(sketch, "E105.right", {"start": v(-1625.6, -736.6) * mm, "end": v(-1625.6, -1092.2) * mm});
            skLineSegment(sketch, "E106.bottom", {"start": v(-1803.4, -1117.6) * mm, "end": v(-1625.6, -1117.6) * mm});
            skLineSegment(sketch, "E106.top", {"start": v(-1803.4, -1295.4) * mm, "end": v(-1625.6, -1295.4) * mm});
            skLineSegment(sketch, "E106.left", {"start": v(-1803.4, -1117.6) * mm, "end": v(-1803.4, -1295.4) * mm});
            skLineSegment(sketch, "E106.right", {"start": v(-1625.6, -1117.6) * mm, "end": v(-1625.6, -1295.4) * mm});
            skLineSegment(sketch, "E107.bottom", {"start": v(-1803.4, -1320.8) * mm, "end": v(-1625.6, -1320.8) * mm});
            skLineSegment(sketch, "E107.top", {"start": v(-1803.4, -1498.6) * mm, "end": v(-1625.6, -1498.6) * mm});
            skLineSegment(sketch, "E107.left", {"start": v(-1803.4, -1320.8) * mm, "end": v(-1803.4, -1498.6) * mm});
            skLineSegment(sketch, "E107.right", {"start": v(-1625.6, -1320.8) * mm, "end": v(-1625.6, -1498.6) * mm});
            skLineSegment(sketch, "E108.bottom", {"start": v(-1803.4, -1524) * mm, "end": v(-1625.6, -1524) * mm});
            skLineSegment(sketch, "E108.top", {"start": v(-1803.4, -1651) * mm, "end": v(-1625.6, -1651) * mm});
            skLineSegment(sketch, "E108.left", {"start": v(-1803.4, -1524) * mm, "end": v(-1803.4, -1651) * mm});
            skLineSegment(sketch, "E108.right", {"start": v(-1625.6, -1524) * mm, "end": v(-1625.6, -1651) * mm});
            skLineSegment(sketch, "E109.bottom", {"start": v(-1397, -177.8) * mm, "end": v(-1219.2, -177.8) * mm});
            skLineSegment(sketch, "E109.top", {"start": v(-1397, -304.8) * mm, "end": v(-1219.2, -304.8) * mm});
            skLineSegment(sketch, "E109.left", {"start": v(-1397, -177.8) * mm, "end": v(-1397, -304.8) * mm});
            skLineSegment(sketch, "E109.right", {"start": v(-1219.2, -177.8) * mm, "end": v(-1219.2, -304.8) * mm});
            skLineSegment(sketch, "E110.bottom", {"start": v(-1600.2, -304.8) * mm, "end": v(-1422.4, -304.8) * mm});
            skLineSegment(sketch, "E110.top", {"start": v(-1600.2, -177.8) * mm, "end": v(-1422.4, -177.8) * mm});
            skLineSegment(sketch, "E110.left", {"start": v(-1600.2, -304.8) * mm, "end": v(-1600.2, -177.8) * mm});
            skLineSegment(sketch, "E110.right", {"start": v(-1422.4, -304.8) * mm, "end": v(-1422.4, -177.8) * mm});
            skLineSegment(sketch, "E111.bottom", {"start": v(-1193.8, -177.8) * mm, "end": v(-1016, -177.8) * mm});
            skLineSegment(sketch, "E111.top", {"start": v(-1193.8, -304.8) * mm, "end": v(-1016, -304.8) * mm});
            skLineSegment(sketch, "E111.left", {"start": v(-1193.8, -177.8) * mm, "end": v(-1193.8, -304.8) * mm});
            skLineSegment(sketch, "E111.right", {"start": v(-1016, -177.8) * mm, "end": v(-1016, -304.8) * mm});
            skLineSegment(sketch, "E112.bottom", {"start": v(-990.6, -177.8) * mm, "end": v(-812.8, -177.8) * mm});
            skLineSegment(sketch, "E112.top", {"start": v(-990.6, -304.8) * mm, "end": v(-812.8, -304.8) * mm});
            skLineSegment(sketch, "E112.left", {"start": v(-990.6, -177.8) * mm, "end": v(-990.6, -304.8) * mm});
            skLineSegment(sketch, "E112.right", {"start": v(-812.8, -177.8) * mm, "end": v(-812.8, -304.8) * mm});
            skLineSegment(sketch, "E113.bottom", {"start": v(-787.4, -177.8) * mm, "end": v(-609.6, -177.8) * mm});
            skLineSegment(sketch, "E113.top", {"start": v(-787.4, -304.8) * mm, "end": v(-609.6, -304.8) * mm});
            skLineSegment(sketch, "E113.left", {"start": v(-787.4, -177.8) * mm, "end": v(-787.4, -304.8) * mm});
            skLineSegment(sketch, "E113.right", {"start": v(-609.6, -177.8) * mm, "end": v(-609.6, -304.8) * mm});
            skLineSegment(sketch, "E114.bottom", {"start": v(-584.2, -177.8) * mm, "end": v(-406.4, -177.8) * mm});
            skLineSegment(sketch, "E114.top", {"start": v(-584.2, -304.8) * mm, "end": v(-406.4, -304.8) * mm});
            skLineSegment(sketch, "E114.left", {"start": v(-584.2, -177.8) * mm, "end": v(-584.2, -304.8) * mm});
            skLineSegment(sketch, "E114.right", {"start": v(-406.4, -177.8) * mm, "end": v(-406.4, -304.8) * mm});
            skLineSegment(sketch, "E115.bottom", {"start": v(-381, -177.8) * mm, "end": v(-203.2, -177.8) * mm});
            skLineSegment(sketch, "E115.top", {"start": v(-381, -304.8) * mm, "end": v(-203.2, -304.8) * mm});
            skLineSegment(sketch, "E115.left", {"start": v(-381, -177.8) * mm, "end": v(-381, -304.8) * mm});
            skLineSegment(sketch, "E115.right", {"start": v(-203.2, -177.8) * mm, "end": v(-203.2, -304.8) * mm});
            skLineSegment(sketch, "E116.bottom", {"start": v(-203.2, -330.2) * mm, "end": v(-381, -330.2) * mm});
            skLineSegment(sketch, "E116.top", {"start": v(-203.2, -508) * mm, "end": v(-381, -508) * mm});
            skLineSegment(sketch, "E116.left", {"start": v(-203.2, -330.2) * mm, "end": v(-203.2, -508) * mm});
            skLineSegment(sketch, "E116.right", {"start": v(-381, -330.2) * mm, "end": v(-381, -508) * mm});
            skLineSegment(sketch, "E117.bottom", {"start": v(-381, -533.4) * mm, "end": v(-203.2, -533.4) * mm});
            skLineSegment(sketch, "E117.top", {"start": v(-381, -711.2) * mm, "end": v(-203.2, -711.2) * mm});
            skLineSegment(sketch, "E117.left", {"start": v(-381, -533.4) * mm, "end": v(-381, -711.2) * mm});
            skLineSegment(sketch, "E117.right", {"start": v(-203.2, -533.4) * mm, "end": v(-203.2, -711.2) * mm});
            skLineSegment(sketch, "E118.bottom", {"start": v(-203.2, -736.6) * mm, "end": v(-381, -736.6) * mm});
            skLineSegment(sketch, "E118.top", {"start": v(-203.2, -1092.2) * mm, "end": v(-381, -1092.2) * mm});
            skLineSegment(sketch, "E118.left", {"start": v(-203.2, -736.6) * mm, "end": v(-203.2, -1092.2) * mm});
            skLineSegment(sketch, "E118.right", {"start": v(-381, -736.6) * mm, "end": v(-381, -1092.2) * mm});
            skLineSegment(sketch, "E119.bottom", {"start": v(-203.2, -1117.6) * mm, "end": v(-381, -1117.6) * mm});
            skLineSegment(sketch, "E119.top", {"start": v(-203.2, -1295.4) * mm, "end": v(-381, -1295.4) * mm});
            skLineSegment(sketch, "E119.left", {"start": v(-203.2, -1117.6) * mm, "end": v(-203.2, -1295.4) * mm});
            skLineSegment(sketch, "E119.right", {"start": v(-381, -1117.6) * mm, "end": v(-381, -1295.4) * mm});
            skLineSegment(sketch, "E120.bottom", {"start": v(-203.2, -1320.8) * mm, "end": v(-381, -1320.8) * mm});
            skLineSegment(sketch, "E120.top", {"start": v(-203.2, -1498.6) * mm, "end": v(-381, -1498.6) * mm});
            skLineSegment(sketch, "E120.left", {"start": v(-203.2, -1320.8) * mm, "end": v(-203.2, -1498.6) * mm});
            skLineSegment(sketch, "E120.right", {"start": v(-381, -1320.8) * mm, "end": v(-381, -1498.6) * mm});
            skLineSegment(sketch, "E121.bottom", {"start": v(-381, -1524) * mm, "end": v(-203.2, -1524) * mm});
            skLineSegment(sketch, "E121.top", {"start": v(-381, -1651) * mm, "end": v(-203.2, -1651) * mm});
            skLineSegment(sketch, "E121.left", {"start": v(-381, -1524) * mm, "end": v(-381, -1651) * mm});
            skLineSegment(sketch, "E121.right", {"start": v(-203.2, -1524) * mm, "end": v(-203.2, -1651) * mm});
            skLineSegment(sketch, "E122.bottom", {"start": v(-584.2, -1524) * mm, "end": v(-406.4, -1524) * mm});
            skLineSegment(sketch, "E122.top", {"start": v(-584.2, -1651) * mm, "end": v(-406.4, -1651) * mm});
            skLineSegment(sketch, "E122.left", {"start": v(-584.2, -1524) * mm, "end": v(-584.2, -1651) * mm});
            skLineSegment(sketch, "E122.right", {"start": v(-406.4, -1524) * mm, "end": v(-406.4, -1651) * mm});
            skLineSegment(sketch, "E123.bottom", {"start": v(-609.6, -1524) * mm, "end": v(-787.4, -1524) * mm});
            skLineSegment(sketch, "E123.top", {"start": v(-609.6, -1651) * mm, "end": v(-787.4, -1651) * mm});
            skLineSegment(sketch, "E123.left", {"start": v(-609.6, -1524) * mm, "end": v(-609.6, -1651) * mm});
            skLineSegment(sketch, "E123.right", {"start": v(-787.4, -1524) * mm, "end": v(-787.4, -1651) * mm});
            skLineSegment(sketch, "E124.bottom", {"start": v(-990.6, -1524) * mm, "end": v(-812.8, -1524) * mm});
            skLineSegment(sketch, "E124.top", {"start": v(-990.6, -1651) * mm, "end": v(-812.8, -1651) * mm});
            skLineSegment(sketch, "E124.left", {"start": v(-990.6, -1524) * mm, "end": v(-990.6, -1651) * mm});
            skLineSegment(sketch, "E124.right", {"start": v(-812.8, -1524) * mm, "end": v(-812.8, -1651) * mm});
            skLineSegment(sketch, "E125.bottom", {"start": v(-1193.8, -1524) * mm, "end": v(-1016, -1524) * mm});
            skLineSegment(sketch, "E125.top", {"start": v(-1193.8, -1651) * mm, "end": v(-1016, -1651) * mm});
            skLineSegment(sketch, "E125.left", {"start": v(-1193.8, -1524) * mm, "end": v(-1193.8, -1651) * mm});
            skLineSegment(sketch, "E125.right", {"start": v(-1016, -1524) * mm, "end": v(-1016, -1651) * mm});
            skLineSegment(sketch, "E126.bottom", {"start": v(-1397, -1524) * mm, "end": v(-1219.2, -1524) * mm});
            skLineSegment(sketch, "E126.top", {"start": v(-1397, -1651) * mm, "end": v(-1219.2, -1651) * mm});
            skLineSegment(sketch, "E126.left", {"start": v(-1397, -1524) * mm, "end": v(-1397, -1651) * mm});
            skLineSegment(sketch, "E126.right", {"start": v(-1219.2, -1524) * mm, "end": v(-1219.2, -1651) * mm});
            skLineSegment(sketch, "E127.bottom", {"start": v(-1422.4, -1524) * mm, "end": v(-1600.2, -1524) * mm});
            skLineSegment(sketch, "E127.top", {"start": v(-1422.4, -1651) * mm, "end": v(-1600.2, -1651) * mm});
            skLineSegment(sketch, "E127.left", {"start": v(-1422.4, -1524) * mm, "end": v(-1422.4, -1651) * mm});
            skLineSegment(sketch, "E127.right", {"start": v(-1600.2, -1524) * mm, "end": v(-1600.2, -1651) * mm});
            skSolve(sketch);
        }
        {
            var Q0;
            Q0 = qSketchRegion(id + "F2", true);
            extrude(context, id + "F3", {"entities" : qUnion([Q0]), "operationType" : NewBodyOperationType.ADD, "depth" : 50.8 * mm});
        }
    });
